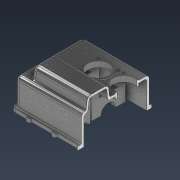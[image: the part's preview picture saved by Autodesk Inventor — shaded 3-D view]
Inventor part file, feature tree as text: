
AUTODESK INVENTOR PART (.ipt)
format: ipt  version: 2022 (Build 260153000, 153)  size: 903,680 bytes
history: native  units: mm
features: extrude x17, sketch x17, fillet x9, plane x3, hole x2, chamfer x2, mirror x1, projected_geometry x1
ambient origin geometry x8: Origin, YZ Plane, XZ Plane, XY Plane, X Axis, Y Axis, Z Axis, Center Point
bodies: Solid1 (feature_tree)
feature tree (52):
  extrude  "Extrusion1"  Depth=350.0mm
  extrude  "Extrusion2"  Depth=10.0mm TaperAngle=0.0deg
  extrude  "Extrusion3"  Depth=10.0mm TaperAngle=0.0deg
  extrude  "Extrusion5"  Depth=68.0mm
  extrude  "Extrusion6"  Depth=23.0mm
  extrude  "Extrusion7"  Depth=50.0mm TaperAngle=0.0deg
  extrude  "Extrusion8"  Depth=108.77mm
  sketch  "Sketch7"  dims[d33=50.0mm d34=150.0mm d35=0.0mm]
  extrude  "Extrusion9"  TaperAngle=0.0deg  [1 undecoded]
  extrude  "Extrusion10"  Depth=4.0mm TaperAngle=0.0deg
  hole  "Hole5"  [1 undecoded]
  extrude  "Extrusion11"  Depth=15.0mm
  extrude  "Extrusion12"  Depth=2.0mm TaperAngle=0.0deg
  extrude  "Extrusion13"  Depth=4.0mm
  extrude  "Extrusion14"  TaperAngle=0.0deg  [1 undecoded]
  extrude  "Extrusion15"  Depth=40.0mm
  fillet  "Fillet1"  Radius=40.0mm
  fillet  "Fillet2"  Radius=21.76mm
  chamfer  "Chamfer1"  Distance=10.0mm
  fillet  "Fillet3"  Radius=10.0mm
  fillet  "Fillet4"  Radius=75.0mm
  fillet  "Fillet5"  Radius=100.0mm
  fillet  "Fillet8"  Radius=260.0mm
  chamfer  "Chamfer2"  Distance=50.0mm
  plane  "Work Plane1"
  mirror  "Mirror1"
  extrude  "Extrusion16"  Depth=24.0mm
  fillet  "Fillet6"  Radius=30.0mm
  fillet  "Fillet7"  Radius=30.0mm
  fillet  "Fillet9"  Radius=50.0mm
  hole  "Hole6"  [1 undecoded]
  plane  "Work Plane2"
  extrude  "Extrusion17"  Depth=24.0mm
  plane  "Work Plane3"
  extrude  "Extrusion18"  Depth=24.0mm TaperAngle=45.0deg
  sketch  "Sketch2"  dims[d0=290.0mm d1=350.0mm]
  sketch  "Sketch3"  dims[d19=10.0mm d20=20.0mm d21=0.0mm]
  sketch  "Sketch4"  dims[d22=100.0mm d23=0.0mm d24=10.0mm d25=0.0mm]
  sketch  "Sketch5"  dims[d28=23.172mm d29=68.0mm]
  sketch  "Sketch6"  dims[d30=150.0mm d31=0.0mm d32=23.0mm]
  sketch  "Sketch8"  dims[d36=160.67mm d37=108.77mm]
  sketch  "Sketch10"  dims[d38=90.0mm d39=0.0mm d40=0.0mm]
  sketch  "Sketch11"  dims[d41=105.0mm d42=4.0mm d43=20.0mm d44=0.0mm d45=0.0mm]
  sketch  "Sketch12"  dims[d46=121.5mm d47=121.5mm]
  projected_geometry  "Projected Loop1"
  sketch  "Sketch13"  dims[d48=85.5mm d49=15.0mm]
  sketch  "Sketch14"  dims[d50=20.0mm d51=0.0mm d59=2.0mm d60=0.0mm]
  sketch  "Sketch15"  dims[d82=8.376mm d83=17.0mm d84=4.0mm d85=2.0mm d86=90.0deg d87=17.0mm d88=20.594885mm d89=25.0mm]
  sketch  "Sketch16"  dims[d90=70.0mm d91=0.0mm d92=0.0mm]
  sketch  "Sketch17"  dims[d93=132.118mm d94=30.0mm d95=40.0mm d96=21.76mm]
  sketch  "Sketch18"  dims[d97=228.068mm d98=10.0mm d99=0.0mm d100=10.0mm d101=0.0mm d105=75.0mm d106=100.0mm d107=260.0mm d108=50.0mm d109=-0.872665mm]
  sketch  "Sketch19"  dims[d110=5.0mm d111=5.0mm d112=30.0mm d113=30.0mm d114=50.0mm d115=-0.872665mm d116=15.0mm d117=20.0mm d118=5.0mm d119=2.0mm d120=45.0deg d121=10.0mm d122=5.0mm d123=20.0mm d124=5.0mm d125=2.0mm d126=45.0deg d127=50.0mm d128=10.0mm d129=10.0mm d130=10.0mm d131=10.0mm d132=20.0mm d133=28.75mm d134=28.75mm d135=30.0mm d136=30.0mm d137=90.0mm d138=70.0mm d139=110.0mm d140=110.0mm d141=50.0mm d142=90.0mm d143=90.0mm d144=90.0mm d145=15.0mm d146=0.0mm d147=10.0mm d148=10.0mm d149=10.0mm d150=10.0mm d151=10.0mm d152=10.0mm d153=20.0mm d154=5.0mm d155=11.0mm d156=5.0mm d157=8.0mm d158=10.0mm d159=4.0mm d160=2.0mm d161=90.0deg d162=10.0mm d163=20.594885mm d164=122.228mm d165=65.0mm d166=50.0mm d167=80.0mm d168=145.0mm d169=21.0mm d170=0.0mm d171=92.1mm d172=24.0mm d173=0.0mm d68=1.0mm d69=1.0mm d70=1.0mm d71=0.15mm d72=0.25mm d73=0.375mm d74=14.3117mm d75=24.0mm d76=20.594885mm d77=0.0625mm d78=0.75mm d79=0.375mm]
note: 4 required parameter values undecoded (feature->parameter linkage not recoverable at this tier; creation-order binding heuristic only, values carry confidence <= 0.55)
